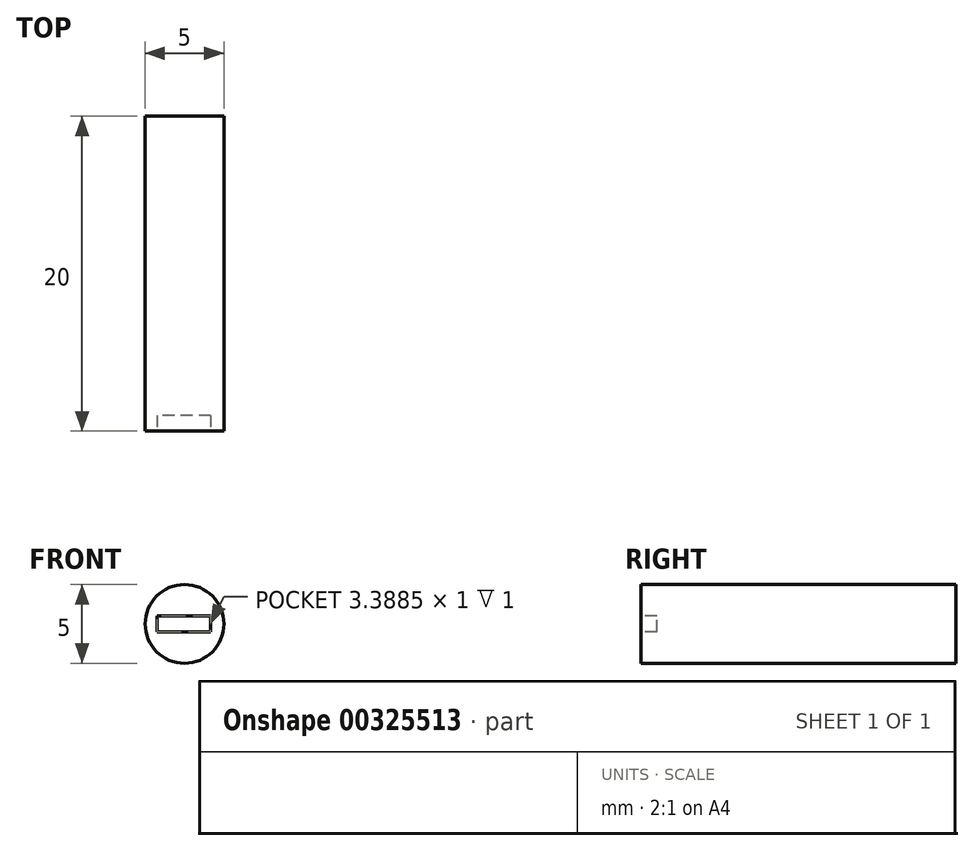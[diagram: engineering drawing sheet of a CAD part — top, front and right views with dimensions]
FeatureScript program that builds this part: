
annotation { "Feature Type Name" : "Feature", "Feature Type Description" : "" }
export const myFeature = defineFeature(function(context is Context, id is Id, definition is map)
    precondition{}
    {
        {
            var Q0;
            Q0=qCreatedBy(makeId("Front.planeOp"),FACE);
            var sketch = newSketch(context, id + "F0", { "sketchPlane" : qUnion([Q0])});
            skCircle(sketch, "E0", {"center": v(0, 0) * mm, "radius": 2.5 * mm});
            skSolve(sketch);
        }
        {
            var Q0;
            Q0 = qSketchRegion(id + "F0", true);
            extrude(context, id + "F1", {"entities" : qUnion([Q0]), "depth" : 20 * mm});
        }
        {
            var Q0;
            Q0=makeQuery(id+"F1.opExtrude","CAP_FACE",FACE,{"disambiguationData":[OSD([sQuery(id+"F0.wireOp",EDGE,"E0")])],"isStart":false});
            var sketch = newSketch(context, id + "F2", { "sketchPlane" : qUnion([Q0])});
            skLineSegment(sketch, "E1", {"start": v(-2.5, 0) * mm, "end": v(2.5, 0) * mm, "construction": true});
            skLineSegment(sketch, "E2.bottom", {"start": v(2.45, -0.5) * mm, "end": v(-2.45, -0.5) * mm});
            skLineSegment(sketch, "E2.top", {"start": v(2.45, 0.5) * mm, "end": v(-2.45, 0.5) * mm});
            skLineSegment(sketch, "E2.left", {"start": v(1.66, -0.5) * mm, "end": v(1.66, 0.5) * mm});
            skLineSegment(sketch, "E2.right", {"start": v(-1.73, -0.5) * mm, "end": v(-1.73, 0.5) * mm});
            skPoint(sketch, "E2.middle", {"position": v(0, 0) * mm});
            skSolve(sketch);
        }
        {
            var Q0;
            Q0 = qSketchRegion(id + "F2", true);
            extrude(context, id + "F3", {"entities" : qUnion([Q0]), "operationType" : NewBodyOperationType.REMOVE, "oppositeDirection" : true, "depth" : 1 * mm});
        }
    });
